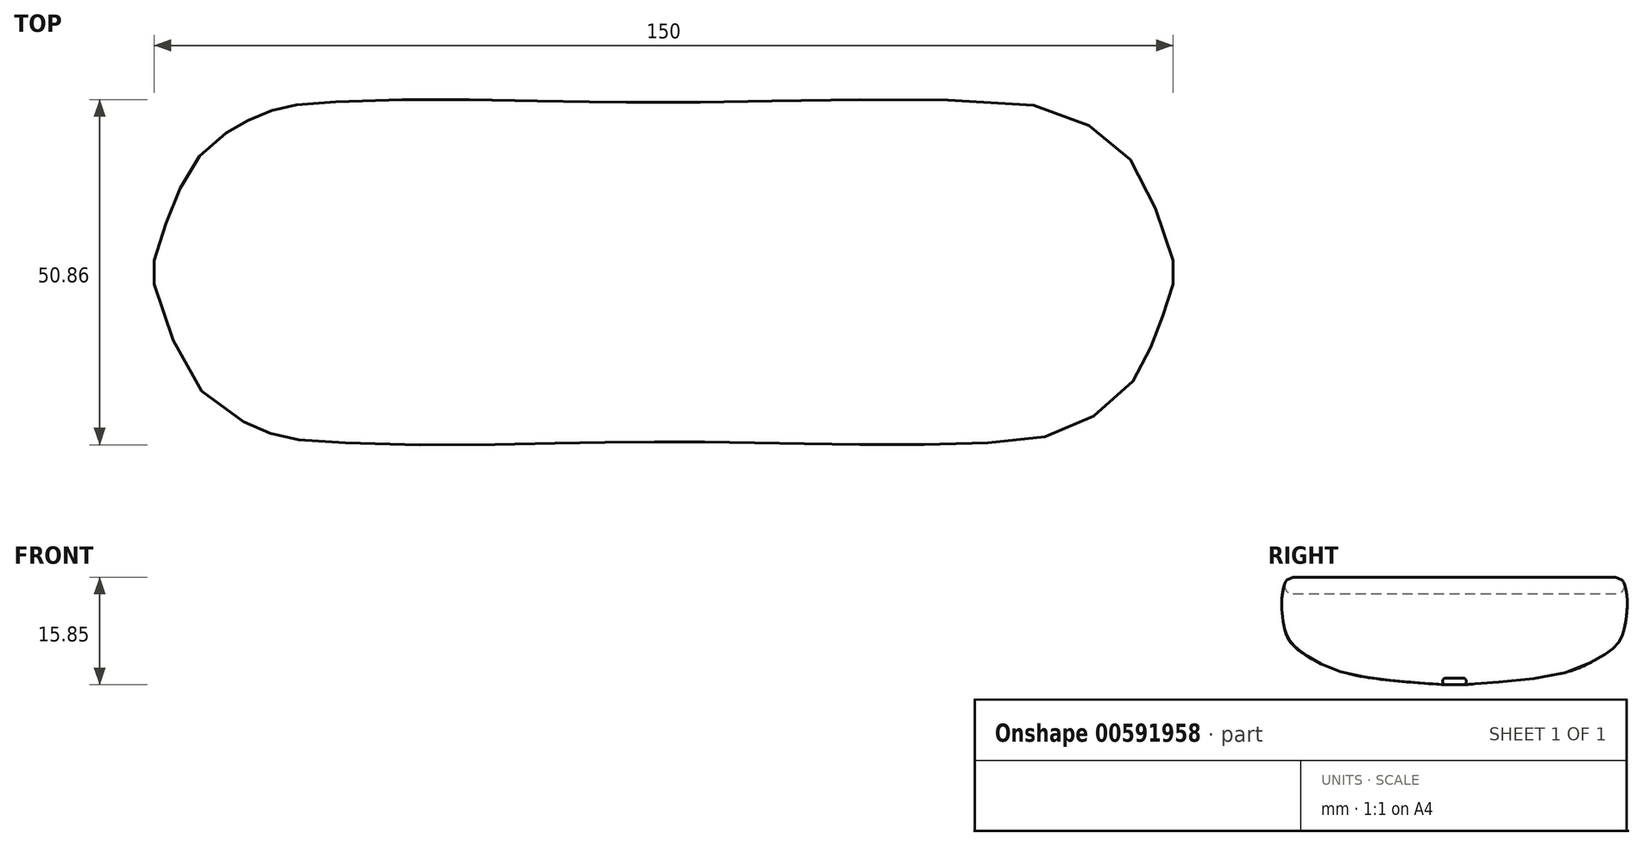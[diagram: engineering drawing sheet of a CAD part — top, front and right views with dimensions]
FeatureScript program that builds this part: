
annotation { "Feature Type Name" : "Feature", "Feature Type Description" : "" }
export const myFeature = defineFeature(function(context is Context, id is Id, definition is map)
    precondition{}
    {
        {
            var Q0;
            Q0=qCreatedBy(makeId("Front.planeOp"),FACE);
            var sketch = newSketch(context, id + "F0", { "sketchPlane" : qUnion([Q0])});
            skArc(sketch, "E0", {"start": v(75, 0) * mm, "mid": v(0, 14.1) * mm, "end": v(-75, 0) * mm});
            skPoint(sketch, "E1", {"position": v(68.75, 2.32) * mm});
            skPoint(sketch, "E2", {"position": v(62.5, 4.41) * mm});
            skPoint(sketch, "E3", {"position": v(56.25, 6.3) * mm});
            skPoint(sketch, "E4", {"position": v(50, 7.95) * mm});
            skPoint(sketch, "E5", {"position": v(0, 14.1) * mm});
            skLineSegment(sketch, "E6", {"start": v(0, 10.44) * mm, "end": v(0, -14.01) * mm});
            skPoint(sketch, "E7.MirrorP", {"position": v(-50, 7.95) * mm});
            skPoint(sketch, "E8.MirrorP", {"position": v(-56.25, 6.3) * mm});
            skPoint(sketch, "E9.MirrorP", {"position": v(-62.5, 4.41) * mm});
            skPoint(sketch, "E10.MirrorP", {"position": v(-68.75, 2.32) * mm});
            skSolve(sketch);
        }
        {
            var Q0;
            Q0=qCreatedBy(makeId("Top.planeOp"),FACE);
            var sketch = newSketch(context, id + "F1", { "sketchPlane" : qUnion([Q0])});
            skLineSegment(sketch, "E11", {"start": v(-50, 0) * mm, "end": v(50, 0) * mm});
            skArc(sketch, "E12.0.startCap", {"start": v(-50, -25) * mm, "mid": v(-75, 0) * mm, "end": v(-50, 25) * mm});
            skArc(sketch, "E12.0.endCap", {"start": v(50, 25) * mm, "mid": v(75, 0) * mm, "end": v(50, -25) * mm});
            skLineSegment(sketch, "E12.0.left", {"start": v(-50, 25) * mm, "end": v(50, 25) * mm});
            skLineSegment(sketch, "E12.0.right", {"start": v(-50, -25) * mm, "end": v(50, -25) * mm});
            skSolve(sketch);
        }
        {
            var Q0;
            Q0=qCreatedBy(makeId("Right.planeOp"),FACE);
            var Q1;
            Q1=sQuery(id+"F0.wireOp",VERTEX,"E0.start");
            cPlane(context, id + "F2", {"entities" : qUnion([Q0, Q1]), "cplaneType" : CPlaneType.PLANE_POINT, "offset" : 25 * mm, "width" : 150 * mm, "height" : 150 * mm});
        }
        {
            var Q0;
            Q0=qCreatedBy(id+"F2.planeOp",FACE);
            var sketch = newSketch(context, id + "F3", { "sketchPlane" : qUnion([Q0])});
            skLineSegment(sketch, "E13", {"start": v(-1.25, 0) * mm, "end": v(1.25, 0) * mm});
            skArc(sketch, "E14.0.startCap", {"start": v(-1.25, -0.5) * mm, "mid": v(-1.75, 0) * mm, "end": v(-1.25, 0.5) * mm});
            skArc(sketch, "E14.0.endCap", {"start": v(1.25, 0.5) * mm, "mid": v(1.75, 0) * mm, "end": v(1.25, -0.5) * mm});
            skLineSegment(sketch, "E14.0.left", {"start": v(-1.25, 0.5) * mm, "end": v(1.25, 0.5) * mm});
            skLineSegment(sketch, "E14.0.right", {"start": v(-1.25, -0.5) * mm, "end": v(1.25, -0.5) * mm});
            skSolve(sketch);
        }
        {
            var Q0;
            Q0=qCreatedBy(id+"F2.planeOp",FACE);
            var Q1;
            Q1=sQuery(id+"F0.wireOp",VERTEX,"E1");
            cPlane(context, id + "F4", {"entities" : qUnion([Q0, Q1]), "cplaneType" : CPlaneType.PLANE_POINT, "offset" : 25 * mm, "width" : 150 * mm, "height" : 150 * mm});
        }
        {
            var Q0;
            Q0=qCreatedBy(id+"F4.planeOp",FACE);
            var Q1;
            Q1=sQuery(id+"F0.wireOp",VERTEX,"E2");
            cPlane(context, id + "F5", {"entities" : qUnion([Q0, Q1]), "cplaneType" : CPlaneType.PLANE_POINT, "offset" : 25 * mm, "width" : 150 * mm, "height" : 150 * mm});
        }
        {
            var Q0;
            Q0=qCreatedBy(id+"F5.planeOp",FACE);
            var Q1;
            Q1=sQuery(id+"F0.wireOp",VERTEX,"E3");
            cPlane(context, id + "F6", {"entities" : qUnion([Q0, Q1]), "cplaneType" : CPlaneType.PLANE_POINT, "offset" : 25 * mm, "width" : 150 * mm, "height" : 150 * mm});
        }
        {
            var Q0;
            Q0=qCreatedBy(id+"F6.planeOp",FACE);
            var Q1;
            Q1=sQuery(id+"F0.wireOp",VERTEX,"E4");
            cPlane(context, id + "F7", {"entities" : qUnion([Q0, Q1]), "cplaneType" : CPlaneType.PLANE_POINT, "offset" : 25 * mm, "width" : 150 * mm, "height" : 150 * mm});
        }
        {
            var Q0;
            Q0=qCreatedBy(id+"F7.planeOp",FACE);
            var Q1;
            Q1=sQuery(id+"F0.wireOp",VERTEX,"E5");
            cPlane(context, id + "F8", {"entities" : qUnion([Q0, Q1]), "cplaneType" : CPlaneType.PLANE_POINT, "offset" : 25 * mm, "width" : 150 * mm, "height" : 150 * mm});
        }
        {
            var Q0;
            Q0=qCreatedBy(id+"F8.planeOp",FACE);
            var Q1;
            Q1=sQuery(id+"F0.wireOp",VERTEX,"E5");
            cPlane(context, id + "F9", {"entities" : qUnion([Q0, Q1]), "cplaneType" : CPlaneType.PLANE_POINT, "offset" : 25 * mm, "width" : 150 * mm, "height" : 150 * mm});
        }
        {
            var Q0;
            Q0=sQuery(id+"F0.wireOp",VERTEX,"E7.MirrorP");
            var Q1;
            Q1=qCreatedBy(makeId("Right.planeOp"),FACE);
            cPlane(context, id + "F10", {"entities" : qUnion([Q0, Q1]), "cplaneType" : CPlaneType.PLANE_POINT, "offset" : 25 * mm, "width" : 150 * mm, "height" : 150 * mm});
        }
        {
            var Q0;
            Q0=sQuery(id+"F0.wireOp",VERTEX,"E8.MirrorP");
            var Q1;
            Q1=qCreatedBy(id+"F10.planeOp",FACE);
            cPlane(context, id + "F11", {"entities" : qUnion([Q0, Q1]), "cplaneType" : CPlaneType.PLANE_POINT, "offset" : 25 * mm, "width" : 150 * mm, "height" : 150 * mm});
        }
        {
            var Q0;
            Q0=sQuery(id+"F0.wireOp",VERTEX,"E9.MirrorP");
            var Q1;
            Q1=qCreatedBy(id+"F10.planeOp",FACE);
            cPlane(context, id + "F12", {"entities" : qUnion([Q0, Q1]), "cplaneType" : CPlaneType.PLANE_POINT, "offset" : 25 * mm, "width" : 150 * mm, "height" : 150 * mm});
        }
        {
            var Q0;
            Q0=sQuery(id+"F0.wireOp",VERTEX,"E10.MirrorP");
            var Q1;
            Q1=qCreatedBy(id+"F12.planeOp",FACE);
            cPlane(context, id + "F13", {"entities" : qUnion([Q0, Q1]), "cplaneType" : CPlaneType.PLANE_POINT, "offset" : 25 * mm, "width" : 150 * mm, "height" : 150 * mm});
        }
        {
            var Q0;
            Q0=sQuery(id+"F1.wireOp",EDGE,"E12.0.startCap");
            cPoint(context, id + "F14", {"entities" : qUnion([Q0]), "parameter" : 0.5});
        }
        {
            var Q0;
            Q0 = qCreatedBy(id + "F14" ,VERTEX);
            var Q1;
            Q1=qCreatedBy(id+"F13.planeOp",FACE);
            cPlane(context, id + "F15", {"entities" : qUnion([Q0, Q1]), "cplaneType" : CPlaneType.PLANE_POINT, "offset" : 25 * mm, "width" : 150 * mm, "height" : 150 * mm});
        }
        {
            var Q0;
            Q0=qCreatedBy(id+"F4.planeOp",FACE);
            var sketch = newSketch(context, id + "F16", { "sketchPlane" : qUnion([Q0])});
            skLineSegment(sketch, "E15", {"start": v(-15.29, 2.32) * mm, "end": v(15.29, 2.32) * mm});
            skArc(sketch, "E16.0.startCap", {"start": v(-15.29, 1.07) * mm, "mid": v(-16.54, 2.32) * mm, "end": v(-15.29, 3.57) * mm});
            skArc(sketch, "E16.0.endCap", {"start": v(15.29, 3.57) * mm, "mid": v(16.54, 2.32) * mm, "end": v(15.29, 1.07) * mm});
            skLineSegment(sketch, "E16.0.left", {"start": v(-15.29, 3.57) * mm, "end": v(15.29, 3.57) * mm});
            skLineSegment(sketch, "E16.0.right", {"start": v(-15.29, 1.07) * mm, "end": v(15.29, 1.07) * mm});
            skSolve(sketch);
        }
        {
            var Q0;
            Q0=qCreatedBy(id+"F5.planeOp",FACE);
            var sketch = newSketch(context, id + "F17", { "sketchPlane" : qUnion([Q0])});
            skLineSegment(sketch, "E17", {"start": v(-20.4, 4.41) * mm, "end": v(20.4, 4.41) * mm});
            skArc(sketch, "E18.0.startCap", {"start": v(-20.4, 3.16) * mm, "mid": v(-21.65, 4.41) * mm, "end": v(-20.4, 5.66) * mm});
            skArc(sketch, "E18.0.endCap", {"start": v(20.4, 5.66) * mm, "mid": v(21.65, 4.41) * mm, "end": v(20.4, 3.16) * mm});
            skLineSegment(sketch, "E18.0.left", {"start": v(-20.4, 5.66) * mm, "end": v(20.4, 5.66) * mm});
            skLineSegment(sketch, "E18.0.right", {"start": v(-20.4, 3.16) * mm, "end": v(20.4, 3.16) * mm});
            skSolve(sketch);
        }
        {
            var Q0;
            Q0=qCreatedBy(id+"F6.planeOp",FACE);
            var sketch = newSketch(context, id + "F18", { "sketchPlane" : qUnion([Q0])});
            skLineSegment(sketch, "E19", {"start": v(-22.96, 6.39) * mm, "end": v(22.96, 6.2) * mm});
            skArc(sketch, "E20.0.startCap", {"start": v(-22.96, 5.14) * mm, "mid": v(-24.2, 6.4) * mm, "end": v(-22.95, 7.64) * mm});
            skArc(sketch, "E20.0.endCap", {"start": v(22.96, 7.44) * mm, "mid": v(24.2, 6.19) * mm, "end": v(22.95, 4.94) * mm});
            skLineSegment(sketch, "E20.0.left", {"start": v(-22.95, 7.64) * mm, "end": v(22.96, 7.44) * mm});
            skLineSegment(sketch, "E20.0.right", {"start": v(-22.96, 5.14) * mm, "end": v(22.95, 4.94) * mm});
            skSolve(sketch);
        }
        {
            var Q0;
            Q0=qCreatedBy(id+"F7.planeOp",FACE);
            var sketch = newSketch(context, id + "F19", { "sketchPlane" : qUnion([Q0])});
            skLineSegment(sketch, "E21", {"start": v(-23.75, 7.95) * mm, "end": v(23.75, 7.95) * mm});
            skArc(sketch, "E22.0.startCap", {"start": v(-23.75, 6.7) * mm, "mid": v(-25, 7.95) * mm, "end": v(-23.75, 9.2) * mm});
            skArc(sketch, "E22.0.endCap", {"start": v(23.75, 9.2) * mm, "mid": v(25, 7.95) * mm, "end": v(23.75, 6.7) * mm});
            skLineSegment(sketch, "E22.0.left", {"start": v(-23.75, 9.2) * mm, "end": v(23.75, 9.2) * mm});
            skLineSegment(sketch, "E22.0.right", {"start": v(-23.75, 6.7) * mm, "end": v(23.75, 6.7) * mm});
            skSolve(sketch);
        }
        {
            var Q0;
            Q0=qCreatedBy(id+"F8.planeOp",FACE);
            var sketch = newSketch(context, id + "F20", { "sketchPlane" : qUnion([Q0])});
            skLineSegment(sketch, "E23", {"start": v(-23.75, 14.1) * mm, "end": v(23.75, 14.1) * mm});
            skArc(sketch, "E24.0.startCap", {"start": v(-23.75, 12.85) * mm, "mid": v(-25, 14.1) * mm, "end": v(-23.75, 15.35) * mm});
            skArc(sketch, "E24.0.endCap", {"start": v(23.75, 15.35) * mm, "mid": v(25, 14.1) * mm, "end": v(23.75, 12.85) * mm});
            skLineSegment(sketch, "E24.0.left", {"start": v(-23.75, 15.35) * mm, "end": v(23.75, 15.35) * mm});
            skLineSegment(sketch, "E24.0.right", {"start": v(-23.75, 12.85) * mm, "end": v(23.75, 12.85) * mm});
            skSolve(sketch);
        }
        {
            var Q0;
            Q0=qCreatedBy(id+"F10.planeOp",FACE);
            var sketch = newSketch(context, id + "F21", { "sketchPlane" : qUnion([Q0])});
            skLineSegment(sketch, "E25", {"start": v(23.75, 7.95) * mm, "end": v(-23.75, 7.95) * mm});
            skArc(sketch, "E26.0.startCap", {"start": v(23.75, 9.2) * mm, "mid": v(25, 7.95) * mm, "end": v(23.75, 6.7) * mm});
            skArc(sketch, "E26.0.endCap", {"start": v(-23.75, 6.7) * mm, "mid": v(-25, 7.95) * mm, "end": v(-23.75, 9.2) * mm});
            skLineSegment(sketch, "E26.0.left", {"start": v(23.75, 6.7) * mm, "end": v(-23.75, 6.7) * mm});
            skLineSegment(sketch, "E26.0.right", {"start": v(23.75, 9.2) * mm, "end": v(-23.75, 9.2) * mm});
            skSolve(sketch);
        }
        {
            var Q0;
            Q0=qCreatedBy(id+"F11.planeOp",FACE);
            var sketch = newSketch(context, id + "F22", { "sketchPlane" : qUnion([Q0])});
            skLineSegment(sketch, "E27", {"start": v(22.96, 6.3) * mm, "end": v(-22.96, 6.3) * mm});
            skArc(sketch, "E28.0.startCap", {"start": v(22.96, 7.54) * mm, "mid": v(24.2, 6.3) * mm, "end": v(22.96, 5.04) * mm});
            skArc(sketch, "E28.0.endCap", {"start": v(-22.96, 5.04) * mm, "mid": v(-24.2, 6.3) * mm, "end": v(-22.96, 7.54) * mm});
            skLineSegment(sketch, "E28.0.left", {"start": v(22.96, 5.04) * mm, "end": v(-22.96, 5.04) * mm});
            skLineSegment(sketch, "E28.0.right", {"start": v(22.96, 7.54) * mm, "end": v(-22.96, 7.54) * mm});
            skSolve(sketch);
        }
        {
            var Q0;
            Q0=qCreatedBy(id+"F12.planeOp",FACE);
            var sketch = newSketch(context, id + "F23", { "sketchPlane" : qUnion([Q0])});
            skLineSegment(sketch, "E29", {"start": v(20.4, 4.41) * mm, "end": v(-20.4, 4.41) * mm});
            skArc(sketch, "E30.0.startCap", {"start": v(20.4, 5.66) * mm, "mid": v(21.65, 4.41) * mm, "end": v(20.4, 3.16) * mm});
            skArc(sketch, "E30.0.endCap", {"start": v(-20.4, 3.16) * mm, "mid": v(-21.65, 4.41) * mm, "end": v(-20.4, 5.66) * mm});
            skLineSegment(sketch, "E30.0.left", {"start": v(20.4, 3.16) * mm, "end": v(-20.4, 3.16) * mm});
            skLineSegment(sketch, "E30.0.right", {"start": v(20.4, 5.66) * mm, "end": v(-20.4, 5.66) * mm});
            skSolve(sketch);
        }
        {
            var Q0;
            Q0=qCreatedBy(id+"F13.planeOp",FACE);
            var sketch = newSketch(context, id + "F24", { "sketchPlane" : qUnion([Q0])});
            skLineSegment(sketch, "E31", {"start": v(15.29, 2.32) * mm, "end": v(-15.29, 2.32) * mm});
            skArc(sketch, "E32.0.startCap", {"start": v(15.29, 3.57) * mm, "mid": v(16.54, 2.32) * mm, "end": v(15.29, 1.07) * mm});
            skArc(sketch, "E32.0.endCap", {"start": v(-15.29, 1.07) * mm, "mid": v(-16.54, 2.32) * mm, "end": v(-15.29, 3.57) * mm});
            skLineSegment(sketch, "E32.0.left", {"start": v(15.29, 1.07) * mm, "end": v(-15.29, 1.07) * mm});
            skLineSegment(sketch, "E32.0.right", {"start": v(15.29, 3.57) * mm, "end": v(-15.29, 3.57) * mm});
            skSolve(sketch);
        }
        {
            var Q0;
            Q0=qCreatedBy(id+"F15.planeOp",FACE);
            var sketch = newSketch(context, id + "F25", { "sketchPlane" : qUnion([Q0])});
            skLineSegment(sketch, "E33", {"start": v(1.25, 0) * mm, "end": v(-1.25, 0) * mm});
            skArc(sketch, "E34.0.startCap", {"start": v(-1.25, -0.5) * mm, "mid": v(-1.75, 0) * mm, "end": v(-1.25, 0.5) * mm});
            skArc(sketch, "E34.0.endCap", {"start": v(1.25, 0.5) * mm, "mid": v(1.75, 0) * mm, "end": v(1.25, -0.5) * mm});
            skLineSegment(sketch, "E34.0.left", {"start": v(1.25, 0.5) * mm, "end": v(-1.25, 0.5) * mm});
            skLineSegment(sketch, "E34.0.right", {"start": v(1.25, -0.5) * mm, "end": v(-1.25, -0.5) * mm});
            skSolve(sketch);
        }
        {
            var Q0;
            Q0 = qSketchRegion(id + "F3", true);
            var Q1;
            Q1 = qSketchRegion(id + "F16", true);
            var Q2;
            Q2 = qSketchRegion(id + "F17", true);
            var Q3;
            Q3 = qSketchRegion(id + "F18", true);
            var Q4;
            Q4 = qSketchRegion(id + "F19", true);
            var Q5;
            Q5 = qSketchRegion(id + "F20", true);
            var Q6;
            Q6 = qSketchRegion(id + "F21", true);
            var Q7;
            Q7 = qSketchRegion(id + "F22", true);
            var Q8;
            Q8 = qSketchRegion(id + "F23", true);
            var Q9;
            Q9 = qSketchRegion(id + "F24", true);
            var Q10;
            Q10 = qSketchRegion(id + "F25", true);
            loft(context, id + "F26", {"sheetProfilesArray" : [{ "sheetProfileEntities" : qUnion([Q0]) }, { "sheetProfileEntities" : qUnion([Q1]) }, { "sheetProfileEntities" : qUnion([Q2]) }, { "sheetProfileEntities" : qUnion([Q3]) }, { "sheetProfileEntities" : qUnion([Q4]) }, { "sheetProfileEntities" : qUnion([Q5]) }, { "sheetProfileEntities" : qUnion([Q6]) }, { "sheetProfileEntities" : qUnion([Q7]) }, { "sheetProfileEntities" : qUnion([Q8]) }, { "sheetProfileEntities" : qUnion([Q9]) }, { "sheetProfileEntities" : qUnion([Q10]) }]});
        }
    });
